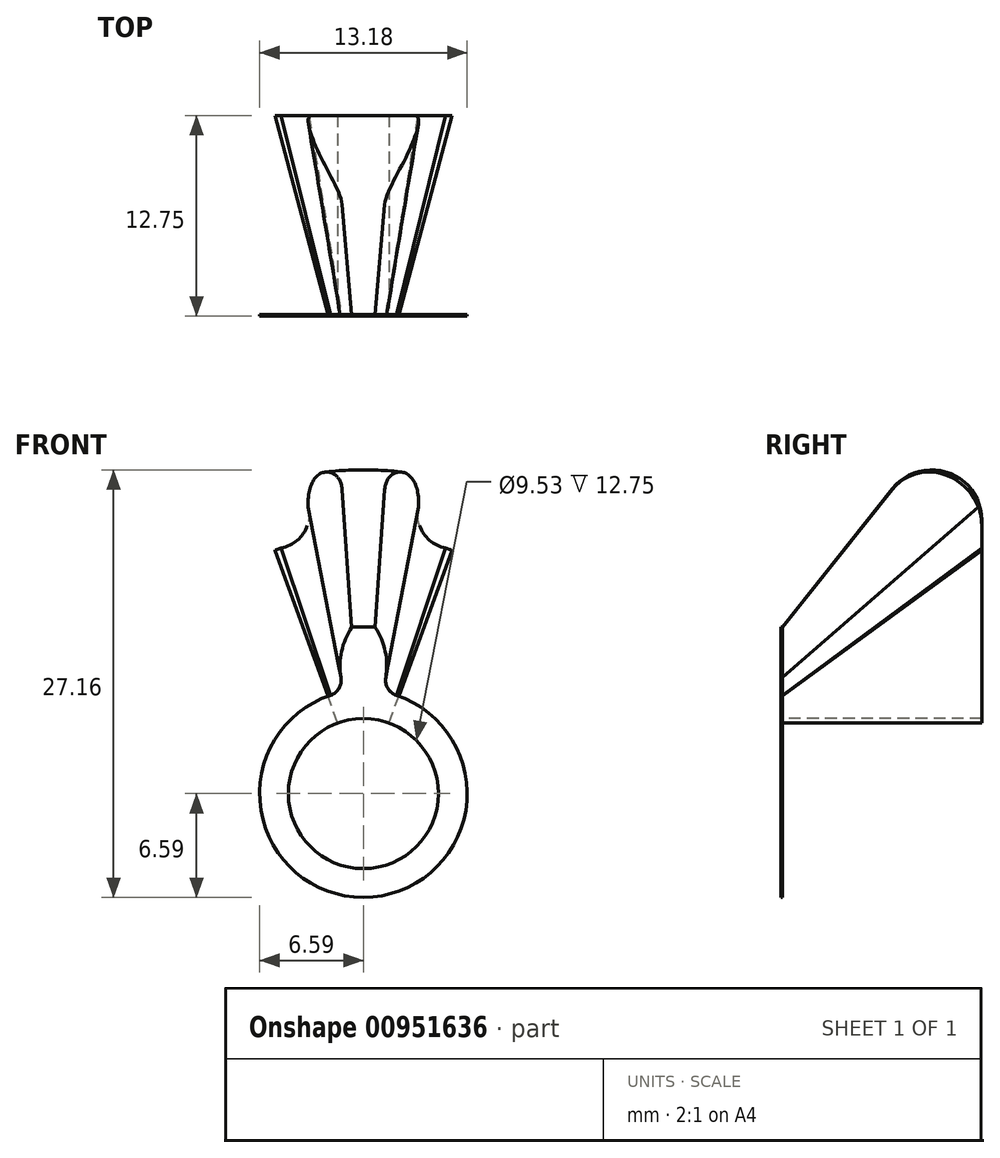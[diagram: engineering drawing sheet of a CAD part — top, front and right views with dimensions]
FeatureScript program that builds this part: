
annotation { "Feature Type Name" : "Feature", "Feature Type Description" : "" }
export const myFeature = defineFeature(function(context is Context, id is Id, definition is map)
    precondition{}
    {
        {
            var Q0;
            Q0=qCreatedBy(makeId("Front.planeOp"),FACE);
            cPlane(context, id + "F0", {"entities" : qUnion([Q0]), "cplaneType" : CPlaneType.OFFSET, "offset" : 12.7 * mm, "oppositeDirection" : true, "width" : 152.4 * mm, "height" : 152.4 * mm});
        }
        {
            assignVariable(context, id + "F1", {"name" : "GearThickness", "anyValue" : .1});
        }
        {
            var Q0;
            Q0=qCreatedBy(makeId("Front.planeOp"),FACE);
            var sketch = newSketch(context, id + "F2", { "sketchPlane" : qUnion([Q0])});
            skCircle(sketch, "E0", {"center": v(0, 0) * mm, "radius": 6.6 * mm});
            skSolve(sketch);
        }
        {
            var Q0;
            Q0=qSketchRegion(id+"F2",true);
            extrude(context, id + "F3", {"entities" : qUnion([Q0]), "endBound" : BoundingType.SYMMETRIC, "offsetDistance" : 25 * mm, "depth" : (getVariable(context, 'GearThickness')) * mm});
        }
        {
            var Q0;
            Q0=qCreatedBy(makeId("Front.planeOp"),FACE);
            var sketch = newSketch(context, id + "F4", { "sketchPlane" : qUnion([Q0])});
            skCircle(sketch, "E1", {"center": v(0, 0) * mm, "radius": 8.6 * mm, "construction": true});
            skLineSegment(sketch, "E2", {"start": v(0, 28.09) * mm, "end": v(0, 0) * mm, "construction": true});
            skLineSegment(sketch, "E3", {"start": v(0, 0) * mm, "end": v(-1.47, 8.46) * mm, "construction": true});
            skLineSegment(sketch, "E4", {"start": v(0, 0) * mm, "end": v(1.47, 8.46) * mm, "construction": true});
            skCircle(sketch, "E5", {"center": v(0, 0) * mm, "radius": 10.6 * mm, "construction": true});
            skArc(sketch, "E6", {"start": v(1.18, 6.48) * mm, "mid": v(0, 6.6) * mm, "end": v(-1.18, 6.48) * mm});
            skArc(sketch, "E7", {"start": v(0.74, 10.56) * mm, "mid": v(0, 10.6) * mm, "end": v(-0.74, 10.56) * mm});
            skLineSegment(sketch, "E8", {"start": v(-1.47, 8.46) * mm, "end": v(-0.72, 17.69) * mm, "construction": true});
            skLineSegment(sketch, "E9", {"start": v(-1.47, 8.46) * mm, "end": v(-0.74, 10.56) * mm, "construction": true});
            skArc(sketch, "E10", {"start": v(-0.74, 10.56) * mm, "mid": v(-1.46, 8.58) * mm, "end": v(-1.18, 6.48) * mm});
            skArc(sketch, "E11", {"start": v(1.18, 6.48) * mm, "mid": v(1.46, 8.58) * mm, "end": v(0.74, 10.56) * mm});
            skSolve(sketch);
        }
        {
            var Q0;
            Q0=qSketchRegion(id+"F4",true);
            extrude(context, id + "F5", {"entities" : qUnion([Q0]), "endBound" : BoundingType.SYMMETRIC, "depth" : (getVariable(context, 'GearThickness')) * mm});
        }
        {
            var Q0;
            Q0=qCreatedBy(makeId("Front.planeOp"),FACE);
            var sketch = newSketch(context, id + "F6", { "sketchPlane" : qUnion([Q0])});
            skArc(sketch, "E12", {"start": v(1.42, 7.36) * mm, "mid": v(1.55, 6.68) * mm, "end": v(2.1, 6.25) * mm});
            skArc(sketch, "E13", {"start": v(-2.1, 6.25) * mm, "mid": v(-1.55, 6.68) * mm, "end": v(-1.42, 7.36) * mm});
            skArc(sketch, "E14", {"start": v(2.1, 6.25) * mm, "mid": v(0, 6.6) * mm, "end": v(-2.1, 6.25) * mm});
            skLineSegment(sketch, "E15", {"start": v(-1.42, 7.36) * mm, "end": v(1.42, 7.36) * mm});
            skSolve(sketch);
        }
        {
            var Q0;
            Q0=qSketchRegion(id+"F6",true);
            extrude(context, id + "F7", {"entities" : qUnion([Q0]), "operationType" : NewBodyOperationType.ADD, "endBound" : BoundingType.SYMMETRIC, "depth" : (getVariable(context, 'GearThickness')) * mm});
        }
        {
            var Q0;
            Q0=makeQuery(id+"F3.opExtrude","CAP_FACE",FACE,{"disambiguationData":[OSD([sQuery(id+"F2.wireOp",EDGE,"E0")])],"isStart":true});
            var sketch = newSketch(context, id + "F8", { "sketchPlane" : qUnion([Q0])});
            skLineSegment(sketch, "E16", {"start": v(0, 0) * mm, "end": v(-2.1, 6.25) * mm, "construction": true});
            skLineSegment(sketch, "E17", {"start": v(0, 0) * mm, "end": v(-1.42, 7.36) * mm, "construction": true});
            skLineSegment(sketch, "E18", {"start": v(0, 0) * mm, "end": v(-0.74, 10.56) * mm, "construction": true});
            skLineSegment(sketch, "E19", {"start": v(0, 0) * mm, "end": v(0.74, 10.56) * mm, "construction": true});
            skLineSegment(sketch, "E20", {"start": v(0, 0) * mm, "end": v(1.42, 7.36) * mm, "construction": true});
            skLineSegment(sketch, "E21", {"start": v(0, 0) * mm, "end": v(2.1, 6.25) * mm, "construction": true});
            skSolve(sketch);
        }
        {
            var Q0;
            Q0=qCreatedBy(makeId("Top.planeOp"),FACE);
            var sketch = newSketch(context, id + "F9", { "sketchPlane" : qUnion([Q0])});
            skLineSegment(sketch, "E22", {"start": v(0, 0) * mm, "end": v(0, 9.45) * mm});
            skSolve(sketch);
        }
        {
            var Q0;
            Q0=sQuery(id+"F9.wireOp",VERTEX,"E22.end");
            var Q1;
            Q1=sQuery(id+"F9.wireOp",VERTEX,"E22.start");
            var Q2;
            Q2=sQuery(id+"F8.wireOp",VERTEX,"E16.end");
            cPlane(context, id + "F10", {"entities" : qUnion([Q0, Q1, Q2]), "cplaneType" : CPlaneType.THREE_POINT, "offset" : 25.4 * mm, "width" : 152.4 * mm, "height" : 152.4 * mm});
        }
        {
            var Q0;
            Q0=qCreatedBy(id+"F10.planeOp",FACE);
            var sketch = newSketch(context, id + "F11", { "sketchPlane" : qUnion([Q0])});
            skLineSegment(sketch, "E23", {"start": v(0.05, 6.59) * mm, "end": v(12.7, 19.24) * mm});
            skSolve(sketch);
        }
        {
            var Q0;
            Q0=sQuery(id+"F8.wireOp",VERTEX,"E20.start");
            var Q1;
            Q1=sQuery(id+"F9.wireOp",VERTEX,"E22.end");
            var Q2;
            Q2=sQuery(id+"F8.wireOp",VERTEX,"E17.end");
            cPlane(context, id + "F12", {"entities" : qUnion([Q0, Q1, Q2]), "cplaneType" : CPlaneType.THREE_POINT, "offset" : 25.4 * mm, "width" : 152.4 * mm, "height" : 152.4 * mm});
        }
        {
            var Q0;
            Q0=qCreatedBy(id+"F12.planeOp",FACE);
            var sketch = newSketch(context, id + "F13", { "sketchPlane" : qUnion([Q0])});
            skLineSegment(sketch, "E24", {"start": v(-0.05, 7.5) * mm, "end": v(-12.7, 20.15) * mm});
            skSolve(sketch);
        }
        {
            var Q0;
            Q0=sQuery(id+"F8.wireOp",VERTEX,"E18.end");
            var Q1;
            Q1=sQuery(id+"F9.wireOp",VERTEX,"E22.end");
            var Q2;
            Q2=sQuery(id+"F9.wireOp",VERTEX,"E22.start");
            cPlane(context, id + "F14", {"entities" : qUnion([Q0, Q1, Q2]), "cplaneType" : CPlaneType.THREE_POINT, "offset" : 25.4 * mm, "width" : 152.4 * mm, "height" : 152.4 * mm});
        }
        {
            var Q0;
            Q0=qCreatedBy(id+"F14.planeOp",FACE);
            var sketch = newSketch(context, id + "F15", { "sketchPlane" : qUnion([Q0])});
            skLineSegment(sketch, "E25", {"start": v(0.05, 10.59) * mm, "end": v(12.7, 23.24) * mm});
            skSolve(sketch);
        }
        {
            var Q0;
            Q0=sQuery(id+"F8.wireOp",VERTEX,"E20.start");
            var Q1;
            Q1=sQuery(id+"F8.wireOp",VERTEX,"E19.end");
            var Q2;
            Q2=sQuery(id+"F9.wireOp",VERTEX,"E22.end");
            cPlane(context, id + "F16", {"entities" : qUnion([Q0, Q1, Q2]), "cplaneType" : CPlaneType.THREE_POINT, "offset" : 25.4 * mm, "width" : 152.4 * mm, "height" : 152.4 * mm});
        }
        {
            var Q0;
            Q0=qCreatedBy(id+"F16.planeOp",FACE);
            var sketch = newSketch(context, id + "F17", { "sketchPlane" : qUnion([Q0])});
            skLineSegment(sketch, "E26", {"start": v(0.05, 10.59) * mm, "end": v(12.7, 23.24) * mm});
            skSolve(sketch);
        }
        {
            var Q0;
            Q0=sQuery(id+"F9.wireOp",VERTEX,"E22.end");
            var Q1;
            Q1=sQuery(id+"F9.wireOp",VERTEX,"E22.start");
            var Q2;
            Q2=sQuery(id+"F8.wireOp",VERTEX,"E20.end");
            cPlane(context, id + "F18", {"entities" : qUnion([Q0, Q1, Q2]), "cplaneType" : CPlaneType.THREE_POINT, "offset" : 25.4 * mm, "width" : 152.4 * mm, "height" : 152.4 * mm});
        }
        {
            var Q0;
            Q0=qCreatedBy(id+"F18.planeOp",FACE);
            var sketch = newSketch(context, id + "F19", { "sketchPlane" : qUnion([Q0])});
            skLineSegment(sketch, "E27", {"start": v(0.05, 7.5) * mm, "end": v(12.7, 20.15) * mm});
            skSolve(sketch);
        }
        {
            var Q0;
            Q0=sQuery(id+"F9.wireOp",VERTEX,"E22.end");
            var Q1;
            Q1=sQuery(id+"F8.wireOp",VERTEX,"E21.end");
            var Q2;
            Q2=sQuery(id+"F9.wireOp",VERTEX,"E22.start");
            cPlane(context, id + "F20", {"entities" : qUnion([Q0, Q1, Q2]), "cplaneType" : CPlaneType.THREE_POINT, "offset" : 25.4 * mm, "width" : 152.4 * mm, "height" : 152.4 * mm});
        }
        {
            var Q0;
            Q0=qCreatedBy(id+"F20.planeOp",FACE);
            var sketch = newSketch(context, id + "F21", { "sketchPlane" : qUnion([Q0])});
            skLineSegment(sketch, "E28", {"start": v(-0.05, 6.6) * mm, "end": v(-12.7, 19.24) * mm});
            skSolve(sketch);
        }
        {
            var Q0;
            Q0=qCreatedBy(id+"F0.planeOp",FACE);
            var sketch = newSketch(context, id + "F22", { "sketchPlane" : qUnion([Q0])});
            skArc(sketch, "E29", {"start": v(1.85, 26.41) * mm, "mid": v(0, 26.48) * mm, "end": v(-1.85, 26.41) * mm});
            skArc(sketch, "E30", {"start": v(-1.85, 26.41) * mm, "mid": v(-3.25, 22.52) * mm, "end": v(-3.55, 18.4) * mm});
            skArc(sketch, "E31", {"start": v(3.55, 18.4) * mm, "mid": v(3.25, 22.52) * mm, "end": v(1.85, 26.41) * mm});
            skArc(sketch, "E32", {"start": v(-5.22, 15.6) * mm, "mid": v(-3.75, 16.62) * mm, "end": v(-3.55, 18.4) * mm});
            skArc(sketch, "E33", {"start": v(3.55, 18.4) * mm, "mid": v(3.75, 16.62) * mm, "end": v(5.22, 15.6) * mm});
            skLineSegment(sketch, "E34", {"start": v(0, 0) * mm, "end": v(-5.22, 15.6) * mm, "construction": true});
            skLineSegment(sketch, "E35", {"start": v(0, 0) * mm, "end": v(-3.55, 18.4) * mm, "construction": true});
            skLineSegment(sketch, "E36", {"start": v(0, 0) * mm, "end": v(-1.85, 26.41) * mm, "construction": true});
            skLineSegment(sketch, "E37", {"start": v(0, 0) * mm, "end": v(1.85, 26.41) * mm, "construction": true});
            skLineSegment(sketch, "E38", {"start": v(0, 0) * mm, "end": v(3.55, 18.4) * mm, "construction": true});
            skLineSegment(sketch, "E39", {"start": v(0, 0) * mm, "end": v(5.22, 15.6) * mm, "construction": true});
            skLineSegment(sketch, "E40", {"start": v(0, 0) * mm, "end": v(5.63, 15.45) * mm});
            skLineSegment(sketch, "E41", {"start": v(0, 0) * mm, "end": v(-5.63, 15.45) * mm});
            skLineSegment(sketch, "E42", {"start": v(0, 0) * mm, "end": v(0, 20.32) * mm, "construction": true});
            skArc(sketch, "E43", {"start": v(-5.22, 15.6) * mm, "mid": v(-5.42, 15.53) * mm, "end": v(-5.63, 15.45) * mm});
            skArc(sketch, "E44", {"start": v(5.63, 15.45) * mm, "mid": v(5.42, 15.53) * mm, "end": v(5.22, 15.6) * mm});
            skSolve(sketch);
        }
        {
            var Q0;
            Q0=makeQuery(id+"F8.imprint","IMPRINT",FACE,{"disambiguationData":[TD([[makeQuery(id+"F8.imprint","IMPRINT",EDGE,{"derivedFrom":makeQuery(id+"F3.opExtrude","CAP_EDGE",EDGE,{"disambiguationData":[OSD([sQuery(id+"F2.wireOp",EDGE,"E0")])],"isStart":true})}),-1.0]])]});
            var sketch = newSketch(context, id + "F23", { "sketchPlane" : qUnion([Q0])});
            skLineSegment(sketch, "E45", {"start": v(0, 0) * mm, "end": v(-2.1, 6.25) * mm, "construction": true});
            skLineSegment(sketch, "E46", {"start": v(0, 0) * mm, "end": v(2.1, 6.25) * mm, "construction": true});
            skArc(sketch, "E47.0", {"start": v(-1.42, 7.36) * mm, "mid": v(-1.55, 6.68) * mm, "end": v(-2.1, 6.25) * mm});
            skArc(sketch, "E47.1", {"start": v(2.1, 6.25) * mm, "mid": v(1.55, 6.68) * mm, "end": v(1.42, 7.36) * mm});
            skArc(sketch, "E47.2", {"start": v(0.74, 10.56) * mm, "mid": v(1.39, 9.03) * mm, "end": v(1.42, 7.36) * mm});
            skArc(sketch, "E47.3", {"start": v(-0.74, 10.56) * mm, "mid": v(0, 10.59) * mm, "end": v(0.74, 10.56) * mm});
            skArc(sketch, "E47.4", {"start": v(-1.42, 7.36) * mm, "mid": v(-1.39, 9.03) * mm, "end": v(-0.74, 10.56) * mm});
            skLineSegment(sketch, "E48", {"start": v(0, 0) * mm, "end": v(-2.25, 6.2) * mm});
            skLineSegment(sketch, "E49", {"start": v(0, 0) * mm, "end": v(2.25, 6.2) * mm});
            skLineSegment(sketch, "E50", {"start": v(0, 0) * mm, "end": v(0, 6.32) * mm});
            skArc(sketch, "E51", {"start": v(-2.1, 6.25) * mm, "mid": v(-2.17, 6.22) * mm, "end": v(-2.25, 6.2) * mm});
            skArc(sketch, "E52", {"start": v(2.25, 6.2) * mm, "mid": v(2.17, 6.22) * mm, "end": v(2.1, 6.25) * mm});
            skSolve(sketch);
        }
        {
            var Q0;
            Q0=qSketchRegion(id+"F23",true);
            var Q1;
            Q1=qSketchRegion(id+"F22",true);
            loft(context, id + "F24", {"operationType" : NewBodyOperationType.ADD, "sheetProfilesArray" : [{ "sheetProfileEntities" : qUnion([Q0]) }, { "sheetProfileEntities" : qUnion([Q1]) }]});
        }
        {
            var Q0;
            Q0=makeQuery(id+"F24.opLoft","MID_CAP_EDGE",EDGE,{"disambiguationData":[OSD([sQuery(id+"F22.wireOp",EDGE,"E29"),sQuery(id+"F22.wireOp",EDGE,"E30"),sQuery(id+"F22.wireOp",EDGE,"E31")])],"capPos":1.0});
            fillet(context, id + "F25", {"entities" : qUnion([Q0]), "radius" : 3.17 * mm, "tangentPropagation" : true, "allowEdgeOverflow" : false});
        }
        {
            var Q0;
            Q0=makeQuery(id+"F24.boolean.opBoolean","MERGE",FACE,{"derivedFrom":[makeQuery(id+"F3.opExtrude","CAP_FACE",FACE,{"disambiguationData":[OSD([sQuery(id+"F2.wireOp",EDGE,"E0")])],"isStart":false}),makeQuery(id+"F7.boolean.opBoolean","MERGE",FACE,{"derivedFrom":[makeQuery(id+"F5.opExtrude","CAP_FACE",FACE,{"disambiguationData":[OSD([sQuery(id+"F4.wireOp",EDGE,"E6"),sQuery(id+"F4.wireOp",EDGE,"E7"),sQuery(id+"F4.wireOp",EDGE,"E10"),sQuery(id+"F4.wireOp",EDGE,"E11")])],"isStart":false}),makeQuery(id+"F7.opExtrude","CAP_FACE",FACE,{"disambiguationData":[OSD([sQuery(id+"F6.wireOp",EDGE,"E12"),sQuery(id+"F6.wireOp",EDGE,"E13"),sQuery(id+"F6.wireOp",EDGE,"E14"),sQuery(id+"F6.wireOp",EDGE,"E15")])],"isStart":false})]})]});
            var sketch = newSketch(context, id + "F26", { "sketchPlane" : qUnion([Q0])});
            skCircle(sketch, "E53", {"center": v(0, 0) * mm, "radius": 4.76 * mm});
            skSolve(sketch);
        }
        {
            var Q0;
            Q0=qSketchRegion(id+"F26",true);
            extrude(context, id + "F27", {"entities" : qUnion([Q0]), "operationType" : NewBodyOperationType.REMOVE, "endBound" : BoundingType.THROUGH_ALL, "oppositeDirection" : true, "depth" : 25.4 * mm, "offsetDistance" : 25.4 * mm});
        }
    });
